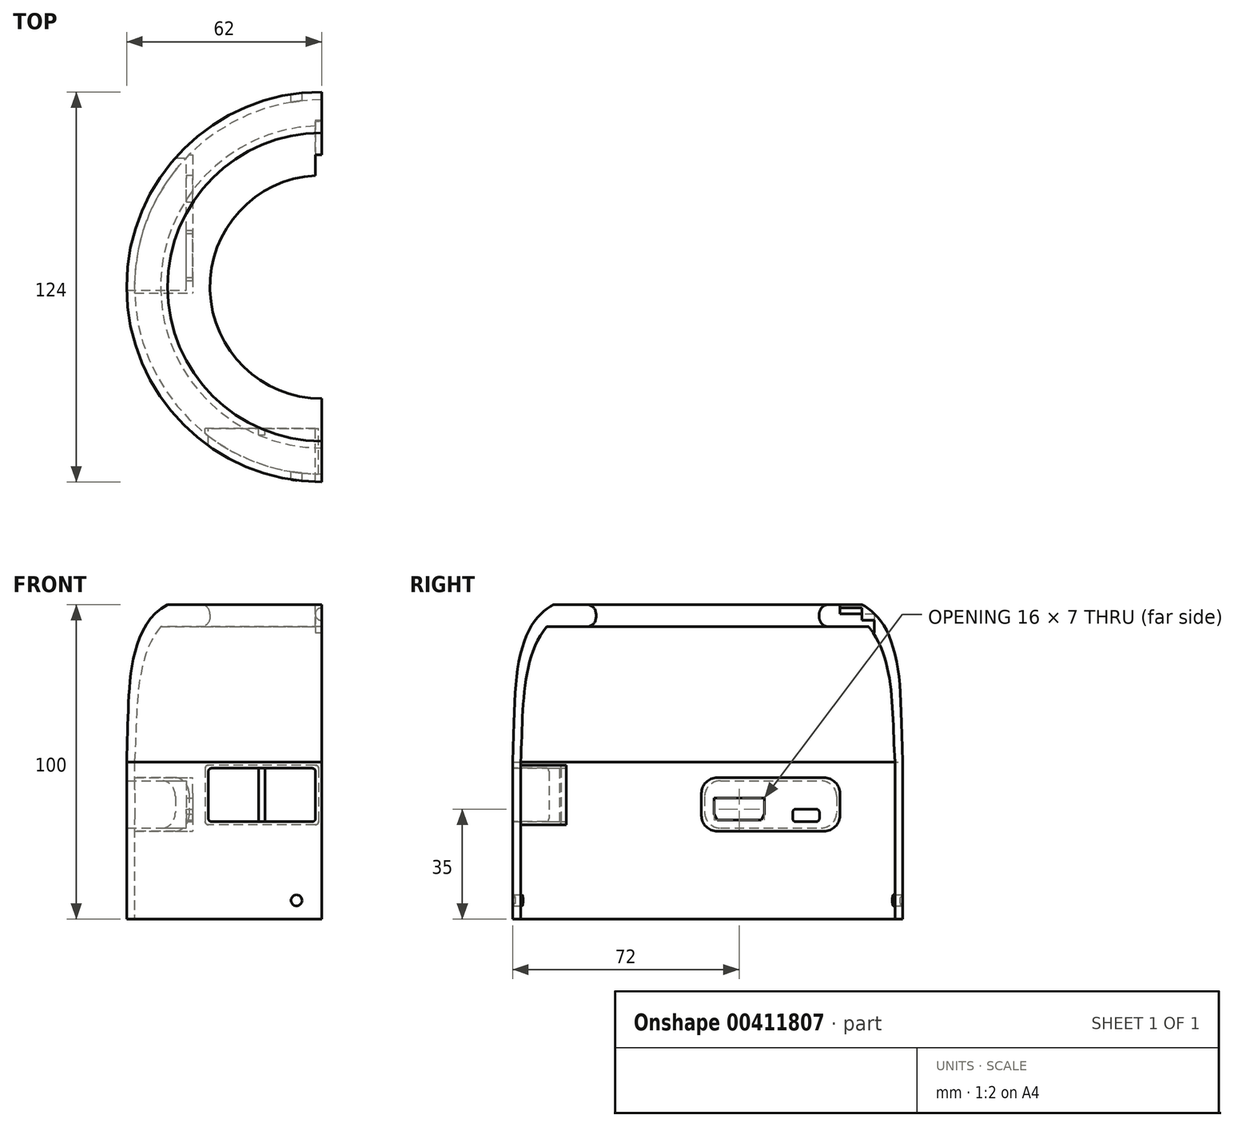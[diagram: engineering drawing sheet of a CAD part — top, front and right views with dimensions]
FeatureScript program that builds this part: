
annotation { "Feature Type Name" : "Feature", "Feature Type Description" : "" }
export const myFeature = defineFeature(function(context is Context, id is Id, definition is map)
    precondition{}
    {
        {
            var Q0;
            Q0=qCreatedBy(makeId("Front.planeOp"),FACE);
            var sketch = newSketch(context, id + "F0", { "sketchPlane" : qUnion([Q0])});
            skLineSegment(sketch, "E0", {"start": v(-38.5, 50) * mm, "end": v(-49, 50) * mm});
            skLineSegment(sketch, "E1", {"start": v(-62, 0) * mm, "end": v(-62, -50) * mm});
            skLineSegment(sketch, "E2", {"start": v(-35.5, 47) * mm, "end": v(-35.5, 46) * mm});
            skLineSegment(sketch, "E3", {"start": v(-38.5, 43) * mm, "end": v(-51.2, 43) * mm});
            skFitSpline(sketch, "E4", {"points": [v(-49, 50) * mm, v(-52.64, 47.47) * mm, v(-56.76, 41.98) * mm, v(-60.39, 29.9) * mm, v(-62, 0) * mm], "startDerivative": vector(-21.37, -10.6) * mm, "endDerivative": vector(-3.86, -109.3) * mm});
            skPoint(sketch, "E5.visualSharp", {"position": v(-35.5, 50) * mm});
            skArc(sketch, "E5.filletArc", {"start": v(-35.5, 47) * mm, "mid": v(-36.38, 49.12) * mm, "end": v(-38.5, 50) * mm});
            skPoint(sketch, "E6.visualSharp", {"position": v(-35.5, 43) * mm});
            skArc(sketch, "E6.filletArc", {"start": v(-38.5, 43) * mm, "mid": v(-36.38, 43.88) * mm, "end": v(-35.5, 46) * mm});
            skLineSegment(sketch, "E7", {"start": v(-62, -50) * mm, "end": v(0, -50) * mm});
            skLineSegment(sketch, "E8", {"start": v(-59.5, -50) * mm, "end": v(-59.5, 0) * mm});
            skFitSpline(sketch, "E9", {"points": [v(-51.2, 43) * mm, v(-59.5, 0) * mm], "startDerivative": vector(-25.81, -31.95) * mm, "endDerivative": vector(-3.04, -46.67) * mm});
            skLineSegment(sketch, "E10", {"start": v(0, -50) * mm, "end": v(0, -45.2) * mm});
            skSolve(sketch);
        }
        {
            var Q0;
            Q0=makeQuery(id+"F0.imprint","IMPRINT",FACE,{"disambiguationData":[TD([[makeQuery(id+"F0.imprint","IMPRINT",EDGE,{"derivedFrom":sQuery(id+"F0.wireOp",EDGE,"E0")}),1.0]])]});
            var Q1;
            Q1=sQuery(id+"F0.wireOp",EDGE,"E10");
            revolve(context, id + "F1", {"entities" : qUnion([Q0]), "axis" : qUnion([Q1]), "revolveType" : RevolveType.SYMMETRIC, "angle" : 180 * degree});
        }
        {
            var Q0;
            Q0=qCreatedBy(makeId("Front.planeOp"),FACE);
            var sketch = newSketch(context, id + "F2", { "sketchPlane" : qUnion([Q0])});
            skCircle(sketch, "E11", {"center": v(0, 47) * mm, "radius": 2 * mm});
            skLineSegment(sketch, "E12", {"start": v(-2, 47.07) * mm, "end": v(-2, 41.07) * mm});
            skLineSegment(sketch, "E13", {"start": v(-2, 41.07) * mm, "end": v(0, 41.07) * mm});
            skLineSegment(sketch, "E14", {"start": v(0, 41.07) * mm, "end": v(0, 45) * mm});
            skLineSegment(sketch, "E15", {"start": v(-2, 47.07) * mm, "end": v(-2, 50.36) * mm});
            skLineSegment(sketch, "E16", {"start": v(0, 50.36) * mm, "end": v(0, 49) * mm});
            skLineSegment(sketch, "E17", {"start": v(-2, 50.36) * mm, "end": v(0, 50.36) * mm});
            skSolve(sketch);
        }
        {
            var Q0;
            {var subQ1=sQuery(id+"F2.wireOp",EDGE,"E11");var subQ4=makeQuery(id+"F2.imprint","INTERSECT",VERTEX,{"derivedFrom":[subQ1,sQuery(id+"F2.wireOp",EDGE,"E14")]});Q0=makeQuery(id+"F2.imprint","IMPRINT",FACE,{"disambiguationData":[TD([[makeQuery(id+"F2.imprint","IMPRINT",EDGE,{"disambiguationData":[TD([[subQ4,1.0]])],"derivedFrom":subQ1}),1.0]])]});}
            extrude(context, id + "F3", {"entities" : qUnion([Q0]), "operationType" : NewBodyOperationType.REMOVE, "oppositeDirection" : true, "depth" : 49 * mm});
        }
        {
            var Q0;
            {var subQ0=sQuery(id+"F2.wireOp",EDGE,"E15");Q0=makeQuery(id+"F2.imprint","IMPRINT",FACE,{"disambiguationData":[TD([[makeQuery(id+"F2.imprint","IMPRINT",EDGE,{"derivedFrom":subQ0}),-1.0]])]});}
            extrude(context, id + "F4", {"entities" : qUnion([Q0]), "operationType" : NewBodyOperationType.REMOVE, "oppositeDirection" : true, "depth" : 42 * mm});
        }
        {
            var Q0;
            {var subQ4=sQuery(id+"F2.wireOp",EDGE,"E13");Q0=makeQuery(id+"F2.imprint","IMPRINT",FACE,{"disambiguationData":[TD([[makeQuery(id+"F2.imprint","IMPRINT",EDGE,{"derivedFrom":subQ4}),1.0]])]});}
            extrude(context, id + "F5", {"entities" : qUnion([Q0]), "operationType" : NewBodyOperationType.REMOVE, "oppositeDirection" : true, "depth" : 53 * mm});
        }
        {
            var Q0;
            Q0=qCreatedBy(makeId("Right.planeOp"),FACE);
            cPlane(context, id + "F6", {"entities" : qUnion([Q0]), "cplaneType" : CPlaneType.OFFSET, "offset" : 41 * mm, "oppositeDirection" : true, "width" : 150 * mm, "height" : 150 * mm});
        }
        {
            var Q0;
            Q0=qCreatedBy(id+"F6.planeOp",FACE);
            var sketch = newSketch(context, id + "F7", { "sketchPlane" : qUnion([Q0])});
            skLineSegment(sketch, "E18.bottom", {"start": v(4, -6) * mm, "end": v(36, -6) * mm});
            skLineSegment(sketch, "E18.top", {"start": v(4, -21) * mm, "end": v(36, -21) * mm});
            skLineSegment(sketch, "E18.left", {"start": v(-1, -11) * mm, "end": v(-1, -16) * mm});
            skLineSegment(sketch, "E18.right", {"start": v(41, -11) * mm, "end": v(41, -16) * mm});
            skPoint(sketch, "E19.visualSharp", {"position": v(-1, -6) * mm});
            skArc(sketch, "E19.filletArc", {"start": v(4, -6) * mm, "mid": v(0.46, -7.46) * mm, "end": v(-1, -11) * mm});
            skPoint(sketch, "E20.visualSharp", {"position": v(41, -6) * mm});
            skArc(sketch, "E20.filletArc", {"start": v(41, -11) * mm, "mid": v(39.54, -7.46) * mm, "end": v(36, -6) * mm});
            skPoint(sketch, "E21.visualSharp", {"position": v(41, -21) * mm});
            skArc(sketch, "E21.filletArc", {"start": v(36, -21) * mm, "mid": v(39.54, -19.54) * mm, "end": v(41, -16) * mm});
            skPoint(sketch, "E22.visualSharp", {"position": v(-1, -21) * mm});
            skArc(sketch, "E22.filletArc", {"start": v(-1, -16) * mm, "mid": v(0.46, -19.54) * mm, "end": v(4, -21) * mm});
            skLineSegment(sketch, "E23", {"start": v(42, -10) * mm, "end": v(42, -17) * mm});
            skLineSegment(sketch, "E24", {"start": v(37, -22) * mm, "end": v(3, -22) * mm});
            skLineSegment(sketch, "E25", {"start": v(37, -5) * mm, "end": v(3, -5) * mm});
            skLineSegment(sketch, "E26", {"start": v(-2, -10) * mm, "end": v(-2, -17) * mm});
            skPoint(sketch, "E27.visualSharp", {"position": v(-2, -5) * mm});
            skArc(sketch, "E27.filletArc", {"start": v(3, -5) * mm, "mid": v(-0.54, -6.46) * mm, "end": v(-2, -10) * mm});
            skPoint(sketch, "E28.visualSharp", {"position": v(42, -5) * mm});
            skArc(sketch, "E28.filletArc", {"start": v(42, -10) * mm, "mid": v(40.54, -6.46) * mm, "end": v(37, -5) * mm});
            skPoint(sketch, "E29.visualSharp", {"position": v(42, -22) * mm});
            skArc(sketch, "E29.filletArc", {"start": v(37, -22) * mm, "mid": v(40.54, -20.54) * mm, "end": v(42, -17) * mm});
            skPoint(sketch, "E30.visualSharp", {"position": v(-2, -22) * mm});
            skArc(sketch, "E30.filletArc", {"start": v(-2, -17) * mm, "mid": v(-0.54, -20.54) * mm, "end": v(3, -22) * mm});
            skSolve(sketch);
        }
        {
            var Q0;
            Q0=makeQuery(id+"F7.imprint","IMPRINT",FACE,{"disambiguationData":[TD([[makeQuery(id+"F7.imprint","IMPRINT",EDGE,{"derivedFrom":sQuery(id+"F7.wireOp",EDGE,"E18.bottom")}),-1.0]])]});
            extrude(context, id + "F8", {"entities" : qUnion([Q0]), "operationType" : NewBodyOperationType.REMOVE, "oppositeDirection" : true, "depth" : 25 * mm});
        }
        {
            var Q0;
            Q0=makeQuery(id+"F7.imprint","IMPRINT",FACE,{"disambiguationData":[TD([[makeQuery(id+"F7.imprint","IMPRINT",EDGE,{"derivedFrom":sQuery(id+"F7.wireOp",EDGE,"E18.bottom")}),1.0]])]});
            var Q1;
            Q1=makeQuery(id+"F1.opRevolve","SWEPT_FACE",FACE,{"disambiguationData":[OSD([sQuery(id+"F0.wireOp",EDGE,"E8")])]});
            extrude(context, id + "F9", {"entities" : qUnion([Q0]), "operationType" : NewBodyOperationType.ADD, "endBound" : BoundingType.UP_TO_SURFACE, "oppositeDirection" : true, "endBoundEntityFace" : qUnion([Q1]), "depth" : 25 * mm});
        }
        {
            var Q0;
            Q0=makeQuery(id+"F7.imprint","IMPRINT",FACE,{"disambiguationData":[TD([[makeQuery(id+"F7.imprint","IMPRINT",EDGE,{"derivedFrom":sQuery(id+"F7.wireOp",EDGE,"E18.bottom")}),-1.0]])]});
            extrude(context, id + "F10", {"entities" : qUnion([Q0]), "operationType" : NewBodyOperationType.ADD, "oppositeDirection" : true, "depth" : 2 * mm});
        }
        {
            var Q0;
            Q0=qCreatedBy(id+"F6.planeOp",FACE);
            var sketch = newSketch(context, id + "F11", { "sketchPlane" : qUnion([Q0])});
            skLineSegment(sketch, "E31.bottom", {"start": v(28, -15) * mm, "end": v(34.5, -15) * mm});
            skLineSegment(sketch, "E31.top", {"start": v(28, -19) * mm, "end": v(34.5, -19) * mm});
            skLineSegment(sketch, "E31.left", {"start": v(27, -16) * mm, "end": v(27, -18) * mm});
            skLineSegment(sketch, "E31.right", {"start": v(35.5, -16) * mm, "end": v(35.5, -18) * mm});
            skLineSegment(sketch, "E32.bottom", {"start": v(2, -11.5) * mm, "end": v(18, -11.5) * mm});
            skLineSegment(sketch, "E32.top", {"start": v(2, -16.5) * mm, "end": v(18, -16.5) * mm});
            skLineSegment(sketch, "E32.left", {"start": v(2, -11.5) * mm, "end": v(2, -16.5) * mm});
            skLineSegment(sketch, "E32.right", {"start": v(18, -11.5) * mm, "end": v(18, -16.5) * mm});
            skLineSegment(sketch, "E33.bottom", {"start": v(3, -11.5) * mm, "end": v(17, -11.5) * mm});
            skLineSegment(sketch, "E33.top", {"start": v(3, -18.5) * mm, "end": v(17, -18.5) * mm});
            skLineSegment(sketch, "E33.left", {"start": v(3, -18.5) * mm, "end": v(3, -11.5) * mm});
            skLineSegment(sketch, "E33.right", {"start": v(17, -18.5) * mm, "end": v(17, -11.5) * mm});
            skLineSegment(sketch, "E34", {"start": v(17, -18.5) * mm, "end": v(18, -16.5) * mm});
            skLineSegment(sketch, "E35", {"start": v(2, -16.5) * mm, "end": v(3, -18.5) * mm});
            skPoint(sketch, "E36.visualSharp", {"position": v(27, -15) * mm});
            skArc(sketch, "E36.filletArc", {"start": v(28, -15) * mm, "mid": v(27.3, -15.3) * mm, "end": v(27, -16) * mm});
            skPoint(sketch, "E37.visualSharp", {"position": v(35.5, -15) * mm});
            skArc(sketch, "E37.filletArc", {"start": v(35.5, -16) * mm, "mid": v(35.2, -15.3) * mm, "end": v(34.5, -15) * mm});
            skPoint(sketch, "E38.visualSharp", {"position": v(35.5, -19) * mm});
            skArc(sketch, "E38.filletArc", {"start": v(34.5, -19) * mm, "mid": v(35.2, -18.7) * mm, "end": v(35.5, -18) * mm});
            skPoint(sketch, "E39.visualSharp", {"position": v(27, -19) * mm});
            skArc(sketch, "E39.filletArc", {"start": v(27, -18) * mm, "mid": v(27.3, -18.7) * mm, "end": v(28, -19) * mm});
            skSolve(sketch);
        }
        {
            var Q0;
            Q0 = qSketchRegion(id + "F11", true);
            extrude(context, id + "F12", {"entities" : qUnion([Q0]), "operationType" : NewBodyOperationType.REMOVE, "oppositeDirection" : true, "depth" : 2 * mm});
        }
        {
            var Q0;
            Q0=qCreatedBy(makeId("Front.planeOp"),FACE);
            cPlane(context, id + "F13", {"entities" : qUnion([Q0]), "cplaneType" : CPlaneType.OFFSET, "offset" : 45 * mm, "width" : 150 * mm, "height" : 150 * mm});
        }
        {
            var Q0;
            Q0=qCreatedBy(id+"F13.planeOp",FACE);
            var sketch = newSketch(context, id + "F14", { "sketchPlane" : qUnion([Q0])});
            skLineSegment(sketch, "E40.bottom", {"start": v(-2, -1) * mm, "end": v(-36, -1) * mm});
            skLineSegment(sketch, "E40.top", {"start": v(-2, -20) * mm, "end": v(-36, -20) * mm});
            skLineSegment(sketch, "E40.left", {"start": v(-1, -2) * mm, "end": v(-1, -19) * mm});
            skLineSegment(sketch, "E40.right", {"start": v(-37, -2) * mm, "end": v(-37, -19) * mm});
            skPoint(sketch, "E41.visualSharp", {"position": v(-1, -1) * mm});
            skArc(sketch, "E41.filletArc", {"start": v(-1, -2) * mm, "mid": v(-1.3, -1.3) * mm, "end": v(-2, -1) * mm});
            skPoint(sketch, "E42.visualSharp", {"position": v(-37, -20) * mm});
            skArc(sketch, "E42.filletArc", {"start": v(-37, -19) * mm, "mid": v(-36.7, -19.7) * mm, "end": v(-36, -20) * mm});
            skPoint(sketch, "E43.visualSharp", {"position": v(-1, -20) * mm});
            skArc(sketch, "E43.filletArc", {"start": v(-2, -20) * mm, "mid": v(-1.3, -19.7) * mm, "end": v(-1, -19) * mm});
            skPoint(sketch, "E44.visualSharp", {"position": v(-37, -1) * mm});
            skArc(sketch, "E44.filletArc", {"start": v(-36, -1) * mm, "mid": v(-36.7, -1.3) * mm, "end": v(-37, -2) * mm});
            skLineSegment(sketch, "E45.bottom", {"start": v(-35, -2) * mm, "end": v(-3, -2) * mm});
            skLineSegment(sketch, "E45.top", {"start": v(-35, -19) * mm, "end": v(-3, -19) * mm});
            skLineSegment(sketch, "E45.left", {"start": v(-36, -3) * mm, "end": v(-36, -18) * mm});
            skLineSegment(sketch, "E45.right", {"start": v(-2, -3) * mm, "end": v(-2, -18) * mm});
            skArc(sketch, "E46.filletArc", {"start": v(-35, -2) * mm, "mid": v(-35.7, -2.3) * mm, "end": v(-36, -3) * mm});
            skArc(sketch, "E47.filletArc", {"start": v(-3, -19) * mm, "mid": v(-2.3, -18.7) * mm, "end": v(-2, -18) * mm});
            skArc(sketch, "E48.filletArc", {"start": v(-36, -18) * mm, "mid": v(-35.7, -18.7) * mm, "end": v(-35, -19) * mm});
            skArc(sketch, "E49.filletArc", {"start": v(-2, -3) * mm, "mid": v(-2.3, -2.3) * mm, "end": v(-3, -2) * mm});
            skLineSegment(sketch, "E50", {"start": v(-20, -19) * mm, "end": v(-20, -2) * mm});
            skLineSegment(sketch, "E51", {"start": v(-18, -2) * mm, "end": v(-18, -19) * mm});
            skSolve(sketch);
        }
        {
            var Q0;
            {var subQ0=sQuery(id+"F14.wireOp",EDGE,"E50");Q0=makeQuery(id+"F14.imprint","IMPRINT",FACE,{"disambiguationData":[TD([[makeQuery(id+"F14.imprint","IMPRINT",EDGE,{"derivedFrom":subQ0}),-1.0]])]});}
            var Q1;
            Q1=makeQuery(id+"F14.imprint","IMPRINT",FACE,{"disambiguationData":[TD([[makeQuery(id+"F14.imprint","IMPRINT",EDGE,{"derivedFrom":sQuery(id+"F14.wireOp",EDGE,"E45.left")}),1.0]])]});
            var Q2;
            Q2=makeQuery(id+"F14.imprint","IMPRINT",FACE,{"disambiguationData":[TD([[makeQuery(id+"F14.imprint","IMPRINT",EDGE,{"derivedFrom":sQuery(id+"F14.wireOp",EDGE,"E45.right")}),-1.0]])]});
            var Q3;
            Q3=makeQuery(id+"F1.opRevolve","SWEPT_FACE",FACE,{"disambiguationData":[OSD([sQuery(id+"F0.wireOp",EDGE,"E1")])]});
            extrude(context, id + "F15", {"entities" : qUnion([Q0, Q1, Q2]), "operationType" : NewBodyOperationType.REMOVE, "endBound" : BoundingType.UP_TO_SURFACE, "endBoundEntityFace" : qUnion([Q3]), "depth" : 25 * mm});
        }
        {
            var Q0;
            Q0=makeQuery(id+"F14.imprint","IMPRINT",FACE,{"disambiguationData":[TD([[makeQuery(id+"F14.imprint","IMPRINT",EDGE,{"derivedFrom":sQuery(id+"F14.wireOp",EDGE,"E40.bottom")}),1.0]])]});
            var Q1;
            Q1=makeQuery(id+"F1.opRevolve","SWEPT_FACE",FACE,{"disambiguationData":[OSD([sQuery(id+"F0.wireOp",EDGE,"E1")])]});
            extrude(context, id + "F16", {"entities" : qUnion([Q0]), "operationType" : NewBodyOperationType.ADD, "endBound" : BoundingType.UP_TO_SURFACE, "endBoundEntityFace" : qUnion([Q1]), "depth" : 25 * mm});
        }
        {
            var Q0;
            {var subQ0=sQuery(id+"F14.wireOp",EDGE,"E50");Q0=makeQuery(id+"F14.imprint","IMPRINT",FACE,{"disambiguationData":[TD([[makeQuery(id+"F14.imprint","IMPRINT",EDGE,{"derivedFrom":subQ0}),-1.0]])]});}
            extrude(context, id + "F17", {"entities" : qUnion([Q0]), "operationType" : NewBodyOperationType.ADD, "depth" : 2 * mm});
        }
        {
            var Q0;
            Q0=qCreatedBy(makeId("Front.planeOp"),FACE);
            var sketch = newSketch(context, id + "F18", { "sketchPlane" : qUnion([Q0])});
            skCircle(sketch, "E52", {"center": v(-8, -44) * mm, "radius": 1.75 * mm});
            skSolve(sketch);
        }
        {
            var Q0;
            Q0=makeQuery(id+"F18.imprint","IMPRINT",FACE,{"disambiguationData":[TD([[makeQuery(id+"F18.imprint","IMPRINT",EDGE,{"derivedFrom":sQuery(id+"F18.wireOp",EDGE,"E52")}),1.0]])]});
            var Q1;
            Q1=sQuery(id+"F18.wireOp",EDGE,"E52");
            extrude(context, id + "F19", {"entities" : qUnion([Q0]), "operationType" : NewBodyOperationType.REMOVE, "surfaceEntities" : qUnion([Q1]), "depth" : 125 * mm, "symmetric" : true});
        }
    });
